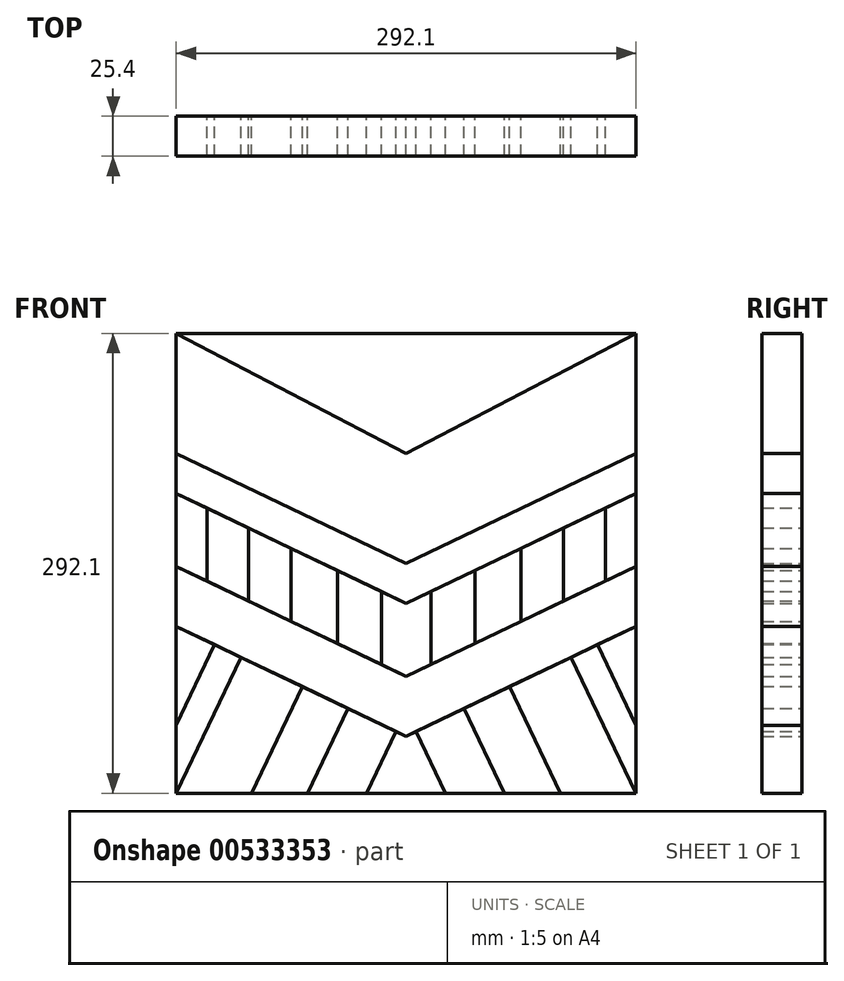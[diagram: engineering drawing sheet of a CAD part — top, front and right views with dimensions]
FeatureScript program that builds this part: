
annotation { "Feature Type Name" : "Feature", "Feature Type Description" : "" }
export const myFeature = defineFeature(function(context is Context, id is Id, definition is map)
    precondition{}
    {
        {
            var Q0;
            Q0=qCreatedBy(makeId("Front.planeOp"),FACE);
            var sketch = newSketch(context, id + "F0", { "sketchPlane" : qUnion([Q0])});
            skLineSegment(sketch, "E0.bottom", {"start": v(-146.05, 146.05) * mm, "end": v(146.05, 146.05) * mm});
            skLineSegment(sketch, "E0.top", {"start": v(-146.05, -146.05) * mm, "end": v(146.05, -146.05) * mm});
            skLineSegment(sketch, "E0.left", {"start": v(-146.05, 146.05) * mm, "end": v(-146.05, -146.05) * mm});
            skLineSegment(sketch, "E0.right", {"start": v(146.05, 146.05) * mm, "end": v(146.05, -146.05) * mm});
            skPoint(sketch, "E0.middle", {"position": v(0, 0) * mm});
            skLineSegment(sketch, "E1", {"start": v(0, 0) * mm, "end": v(0, -109.8) * mm});
            skLineSegment(sketch, "E2", {"start": v(0, 69.85) * mm, "end": v(-146.05, 146.05) * mm});
            skLineSegment(sketch, "E3", {"start": v(0, 69.85) * mm, "end": v(146.05, 146.05) * mm});
            skLineSegment(sketch, "E4", {"start": v(0, 0) * mm, "end": v(-146.05, 69.85) * mm});
            skLineSegment(sketch, "E5", {"start": v(146.05, 69.85) * mm, "end": v(0, 0) * mm});
            skLineSegment(sketch, "E6", {"start": v(0, -71.7) * mm, "end": v(-146.05, -1.85) * mm});
            skLineSegment(sketch, "E7", {"start": v(146.05, -1.85) * mm, "end": v(0, -71.7) * mm});
            skLineSegment(sketch, "E8", {"start": v(0, -109.8) * mm, "end": v(-146.05, -39.95) * mm});
            skLineSegment(sketch, "E9", {"start": v(146.05, -39.95) * mm, "end": v(0, -109.8) * mm});
            skLineSegment(sketch, "E10", {"start": v(0, -25.4) * mm, "end": v(-146.05, 44.45) * mm});
            skLineSegment(sketch, "E11", {"start": v(146.05, 44.45) * mm, "end": v(0, -25.4) * mm});
            skPoint(sketch, "E12.orphan", {"position": v(0, 146.05) * mm});
            skLineSegment(sketch, "E13", {"start": v(-146.05, -102.82) * mm, "end": v(-121.58, -51.65) * mm});
            skLineSegment(sketch, "E14", {"start": v(-146.05, -146.05) * mm, "end": v(-104.75, -59.7) * mm});
            skLineSegment(sketch, "E15", {"start": v(-98.15, -146.05) * mm, "end": v(-65.77, -78.34) * mm});
            skLineSegment(sketch, "E16", {"start": v(-62.61, -146.05) * mm, "end": v(-36.85, -92.18) * mm});
            skLineSegment(sketch, "E17", {"start": v(-25.15, -146.05) * mm, "end": v(-6.36, -106.76) * mm});
            skPoint(sketch, "E18.end.orphan", {"position": v(0, -146.05) * mm});
            skLineSegment(sketch, "E19.MirrorCS", {"start": v(25.15, -146.05) * mm, "end": v(6.36, -106.76) * mm});
            skLineSegment(sketch, "E20.MirrorCS", {"start": v(62.61, -146.05) * mm, "end": v(36.85, -92.18) * mm});
            skLineSegment(sketch, "E21.MirrorCS", {"start": v(98.15, -146.05) * mm, "end": v(65.77, -78.34) * mm});
            skLineSegment(sketch, "E22.MirrorCS", {"start": v(146.05, -146.05) * mm, "end": v(104.75, -59.7) * mm});
            skLineSegment(sketch, "E23.MirrorCS", {"start": v(146.05, -102.82) * mm, "end": v(121.58, -51.65) * mm});
            skLineSegment(sketch, "E24", {"start": v(-126.53, -11.18) * mm, "end": v(-126.53, 35.12) * mm});
            skLineSegment(sketch, "E25", {"start": v(-99.96, -23.9) * mm, "end": v(-99.96, 22.4) * mm});
            skLineSegment(sketch, "E26", {"start": v(-73.03, -36.77) * mm, "end": v(-73.02, 9.53) * mm});
            skLineSegment(sketch, "E27", {"start": v(-43.67, -50.82) * mm, "end": v(-43.67, -4.52) * mm});
            skLineSegment(sketch, "E28", {"start": v(-15.68, -64.2) * mm, "end": v(-15.68, -17.9) * mm});
            skLineSegment(sketch, "E29.MirrorCS", {"start": v(15.68, -64.2) * mm, "end": v(15.68, -17.9) * mm});
            skLineSegment(sketch, "E30.MirrorCS", {"start": v(43.67, -50.82) * mm, "end": v(43.67, -4.52) * mm});
            skLineSegment(sketch, "E31.MirrorCS", {"start": v(73.03, -36.77) * mm, "end": v(73.02, 9.52) * mm});
            skLineSegment(sketch, "E32.MirrorCS", {"start": v(99.96, -23.9) * mm, "end": v(99.96, 22.4) * mm});
            skLineSegment(sketch, "E33.MirrorCS", {"start": v(126.53, -11.18) * mm, "end": v(126.53, 35.12) * mm});
            skSolve(sketch);
        }
        {
            var Q0;
            {var subQ5=sQuery(id+"F0.wireOp",EDGE,"E2");Q0=makeQuery(id+"F0.imprint","IMPRINT",FACE,{"disambiguationData":[TD([[makeQuery(id+"F0.imprint","IMPRINT",EDGE,{"derivedFrom":subQ5}),1.0]])]});}
            extrude(context, id + "F1", {"entities" : qUnion([Q0]), "depth" : 25.4 * mm, "offsetDistance" : 25.4 * mm});
        }
        {
            var Q0;
            Q0=makeQuery(id+"F0.imprint","IMPRINT",FACE,{"disambiguationData":[TD([[makeQuery(id+"F0.imprint","IMPRINT",EDGE,{"derivedFrom":sQuery(id+"F0.wireOp",EDGE,"E0.bottom")}),-1.0]])]});
            extrude(context, id + "F2", {"entities" : qUnion([Q0]), "depth" : 25.4 * mm, "offsetDistance" : 25.4 * mm});
        }
        {
            var Q0;
            {var subQ4=sQuery(id+"F0.wireOp",EDGE,"E5");Q0=makeQuery(id+"F0.imprint","IMPRINT",FACE,{"disambiguationData":[TD([[makeQuery(id+"F0.imprint","IMPRINT",EDGE,{"derivedFrom":subQ4}),1.0]])]});}
            var Q1;
            {var subQ4=sQuery(id+"F0.wireOp",EDGE,"E4");Q1=makeQuery(id+"F0.imprint","IMPRINT",FACE,{"disambiguationData":[TD([[makeQuery(id+"F0.imprint","IMPRINT",EDGE,{"derivedFrom":subQ4}),1.0]])]});}
            extrude(context, id + "F3", {"entities" : qUnion([Q0, Q1]), "depth" : 25.4 * mm, "offsetDistance" : 25.4 * mm});
        }
        {
            var Q0;
            {var subQ5=sQuery(id+"F0.wireOp",EDGE,"E24");Q0=makeQuery(id+"F0.imprint","IMPRINT",FACE,{"disambiguationData":[TD([[makeQuery(id+"F0.imprint","IMPRINT",EDGE,{"derivedFrom":subQ5}),1.0]])]});}
            extrude(context, id + "F4", {"entities" : qUnion([Q0]), "depth" : 25.4 * mm, "offsetDistance" : 25.4 * mm});
        }
        {
            var Q0;
            {var subQ0=sQuery(id+"F0.wireOp",EDGE,"E24");Q0=makeQuery(id+"F0.imprint","IMPRINT",FACE,{"disambiguationData":[TD([[makeQuery(id+"F0.imprint","IMPRINT",EDGE,{"derivedFrom":subQ0}),-1.0]])]});}
            extrude(context, id + "F5", {"entities" : qUnion([Q0]), "depth" : 25.4 * mm, "offsetDistance" : 25.4 * mm});
        }
        {
            var Q0;
            {var subQ0=sQuery(id+"F0.wireOp",EDGE,"E25");Q0=makeQuery(id+"F0.imprint","IMPRINT",FACE,{"disambiguationData":[TD([[makeQuery(id+"F0.imprint","IMPRINT",EDGE,{"derivedFrom":subQ0}),-1.0]])]});}
            extrude(context, id + "F6", {"entities" : qUnion([Q0]), "depth" : 25.4 * mm, "offsetDistance" : 25.4 * mm});
        }
        {
            var Q0;
            {var subQ0=sQuery(id+"F0.wireOp",EDGE,"E26");Q0=makeQuery(id+"F0.imprint","IMPRINT",FACE,{"disambiguationData":[TD([[makeQuery(id+"F0.imprint","IMPRINT",EDGE,{"derivedFrom":subQ0}),-1.0]])]});}
            extrude(context, id + "F7", {"entities" : qUnion([Q0]), "depth" : 25.4 * mm, "offsetDistance" : 25.4 * mm});
        }
        {
            var Q0;
            {var subQ0=sQuery(id+"F0.wireOp",EDGE,"E27");Q0=makeQuery(id+"F0.imprint","IMPRINT",FACE,{"disambiguationData":[TD([[makeQuery(id+"F0.imprint","IMPRINT",EDGE,{"derivedFrom":subQ0}),-1.0]])]});}
            extrude(context, id + "F8", {"entities" : qUnion([Q0]), "depth" : 25.4 * mm, "offsetDistance" : 25.4 * mm});
        }
        {
            var Q0;
            {var subQ5=sQuery(id+"F0.wireOp",EDGE,"E29.MirrorCS");Q0=makeQuery(id+"F0.imprint","IMPRINT",FACE,{"disambiguationData":[TD([[makeQuery(id+"F0.imprint","IMPRINT",EDGE,{"derivedFrom":subQ5}),1.0]])]});}
            var Q1;
            {var subQ5=sQuery(id+"F0.wireOp",EDGE,"E28");Q1=makeQuery(id+"F0.imprint","IMPRINT",FACE,{"disambiguationData":[TD([[makeQuery(id+"F0.imprint","IMPRINT",EDGE,{"derivedFrom":subQ5}),-1.0]])]});}
            extrude(context, id + "F9", {"entities" : qUnion([Q0, Q1]), "depth" : 25.4 * mm, "offsetDistance" : 25.4 * mm});
        }
        {
            var Q0;
            {var subQ0=sQuery(id+"F0.wireOp",EDGE,"E29.MirrorCS");Q0=makeQuery(id+"F0.imprint","IMPRINT",FACE,{"disambiguationData":[TD([[makeQuery(id+"F0.imprint","IMPRINT",EDGE,{"derivedFrom":subQ0}),-1.0]])]});}
            extrude(context, id + "F10", {"entities" : qUnion([Q0]), "depth" : 25.4 * mm, "offsetDistance" : 25.4 * mm});
        }
        {
            var Q0;
            {var subQ0=sQuery(id+"F0.wireOp",EDGE,"E30.MirrorCS");Q0=makeQuery(id+"F0.imprint","IMPRINT",FACE,{"disambiguationData":[TD([[makeQuery(id+"F0.imprint","IMPRINT",EDGE,{"derivedFrom":subQ0}),-1.0]])]});}
            extrude(context, id + "F11", {"entities" : qUnion([Q0]), "depth" : 25.4 * mm, "offsetDistance" : 25.4 * mm});
        }
        {
            var Q0;
            {var subQ0=sQuery(id+"F0.wireOp",EDGE,"E31.MirrorCS");Q0=makeQuery(id+"F0.imprint","IMPRINT",FACE,{"disambiguationData":[TD([[makeQuery(id+"F0.imprint","IMPRINT",EDGE,{"derivedFrom":subQ0}),-1.0]])]});}
            extrude(context, id + "F12", {"entities" : qUnion([Q0]), "depth" : 25.4 * mm, "offsetDistance" : 25.4 * mm});
        }
        {
            var Q0;
            {var subQ0=sQuery(id+"F0.wireOp",EDGE,"E32.MirrorCS");Q0=makeQuery(id+"F0.imprint","IMPRINT",FACE,{"disambiguationData":[TD([[makeQuery(id+"F0.imprint","IMPRINT",EDGE,{"derivedFrom":subQ0}),-1.0]])]});}
            extrude(context, id + "F13", {"entities" : qUnion([Q0]), "depth" : 25.4 * mm, "offsetDistance" : 25.4 * mm});
        }
        {
            var Q0;
            {var subQ5=sQuery(id+"F0.wireOp",EDGE,"E33.MirrorCS");Q0=makeQuery(id+"F0.imprint","IMPRINT",FACE,{"disambiguationData":[TD([[makeQuery(id+"F0.imprint","IMPRINT",EDGE,{"derivedFrom":subQ5}),-1.0]])]});}
            extrude(context, id + "F14", {"entities" : qUnion([Q0]), "depth" : 25.4 * mm, "offsetDistance" : 25.4 * mm});
        }
        {
            var Q0;
            {var subQ0=sQuery(id+"F0.wireOp",EDGE,"E6");var subQ1=sQuery(id+"F0.wireOp",EDGE,"E0.left");var subQ2=makeQuery(id+"F0.imprint","INTERSECT",VERTEX,{"derivedFrom":[subQ1,subQ0]});Q0=makeQuery(id+"F0.imprint","IMPRINT",FACE,{"disambiguationData":[TD([[makeQuery(id+"F0.imprint","IMPRINT",EDGE,{"disambiguationData":[TD([[subQ2,-1.0]])],"derivedFrom":subQ1}),1.0]])]});}
            var Q1;
            {var subQ0=sQuery(id+"F0.wireOp",EDGE,"E7");var subQ10=sQuery(id+"F0.wireOp",EDGE,"E0.right");var subQ11=makeQuery(id+"F0.imprint","INTERSECT",VERTEX,{"derivedFrom":[subQ10,subQ0]});Q1=makeQuery(id+"F0.imprint","IMPRINT",FACE,{"disambiguationData":[TD([[makeQuery(id+"F0.imprint","IMPRINT",EDGE,{"disambiguationData":[TD([[subQ11,-1.0]])],"derivedFrom":subQ10}),-1.0]])]});}
            extrude(context, id + "F15", {"entities" : qUnion([Q0, Q1]), "depth" : 25.4 * mm, "offsetDistance" : 25.4 * mm});
        }
        {
            var Q0;
            {var subQ3=sQuery(id+"F0.wireOp",EDGE,"E13");Q0=makeQuery(id+"F0.imprint","IMPRINT",FACE,{"disambiguationData":[TD([[makeQuery(id+"F0.imprint","IMPRINT",EDGE,{"derivedFrom":subQ3}),1.0]])]});}
            extrude(context, id + "F16", {"entities" : qUnion([Q0]), "depth" : 25.4 * mm, "offsetDistance" : 25.4 * mm});
        }
        {
            var Q0;
            {var subQ2=sQuery(id+"F0.wireOp",EDGE,"E13");Q0=makeQuery(id+"F0.imprint","IMPRINT",FACE,{"disambiguationData":[TD([[makeQuery(id+"F0.imprint","IMPRINT",EDGE,{"derivedFrom":subQ2}),-1.0]])]});}
            extrude(context, id + "F17", {"entities" : qUnion([Q0]), "depth" : 25.4 * mm, "offsetDistance" : 25.4 * mm});
        }
        {
            var Q0;
            {var subQ0=sQuery(id+"F0.wireOp",EDGE,"E14");Q0=makeQuery(id+"F0.imprint","IMPRINT",FACE,{"disambiguationData":[TD([[makeQuery(id+"F0.imprint","IMPRINT",EDGE,{"derivedFrom":subQ0}),-1.0]])]});}
            extrude(context, id + "F18", {"entities" : qUnion([Q0]), "depth" : 25.4 * mm, "offsetDistance" : 25.4 * mm});
        }
        {
            var Q0;
            {var subQ0=sQuery(id+"F0.wireOp",EDGE,"E15");Q0=makeQuery(id+"F0.imprint","IMPRINT",FACE,{"disambiguationData":[TD([[makeQuery(id+"F0.imprint","IMPRINT",EDGE,{"derivedFrom":subQ0}),-1.0]])]});}
            var Q1;
            {var subQ0=sQuery(id+"F0.wireOp",EDGE,"E17");Q1=makeQuery(id+"F0.imprint","IMPRINT",FACE,{"disambiguationData":[TD([[makeQuery(id+"F0.imprint","IMPRINT",EDGE,{"derivedFrom":subQ0}),-1.0]])]});}
            var Q2;
            {var subQ0=sQuery(id+"F0.wireOp",EDGE,"E20.MirrorCS");Q2=makeQuery(id+"F0.imprint","IMPRINT",FACE,{"disambiguationData":[TD([[makeQuery(id+"F0.imprint","IMPRINT",EDGE,{"derivedFrom":subQ0}),-1.0]])]});}
            var Q3;
            {var subQ0=sQuery(id+"F0.wireOp",EDGE,"E22.MirrorCS");Q3=makeQuery(id+"F0.imprint","IMPRINT",FACE,{"disambiguationData":[TD([[makeQuery(id+"F0.imprint","IMPRINT",EDGE,{"derivedFrom":subQ0}),-1.0]])]});}
            extrude(context, id + "F19", {"entities" : qUnion([Q0, Q1, Q2, Q3]), "depth" : 25.4 * mm, "offsetDistance" : 25.4 * mm});
        }
        {
            var Q0;
            {var subQ0=sQuery(id+"F0.wireOp",EDGE,"E16");Q0=makeQuery(id+"F0.imprint","IMPRINT",FACE,{"disambiguationData":[TD([[makeQuery(id+"F0.imprint","IMPRINT",EDGE,{"derivedFrom":subQ0}),-1.0]])]});}
            var Q1;
            {var subQ0=sQuery(id+"F0.wireOp",EDGE,"E19.MirrorCS");Q1=makeQuery(id+"F0.imprint","IMPRINT",FACE,{"disambiguationData":[TD([[makeQuery(id+"F0.imprint","IMPRINT",EDGE,{"derivedFrom":subQ0}),-1.0]])]});}
            var Q2;
            {var subQ2=sQuery(id+"F0.wireOp",EDGE,"E21.MirrorCS");Q2=makeQuery(id+"F0.imprint","IMPRINT",FACE,{"disambiguationData":[TD([[makeQuery(id+"F0.imprint","IMPRINT",EDGE,{"derivedFrom":subQ2}),-1.0]])]});}
            var Q3;
            {var subQ3=sQuery(id+"F0.wireOp",EDGE,"E23.MirrorCS");Q3=makeQuery(id+"F0.imprint","IMPRINT",FACE,{"disambiguationData":[TD([[makeQuery(id+"F0.imprint","IMPRINT",EDGE,{"derivedFrom":subQ3}),-1.0]])]});}
            extrude(context, id + "F20", {"entities" : qUnion([Q0, Q1, Q2, Q3]), "depth" : 25.4 * mm, "offsetDistance" : 25.4 * mm});
        }
    });
